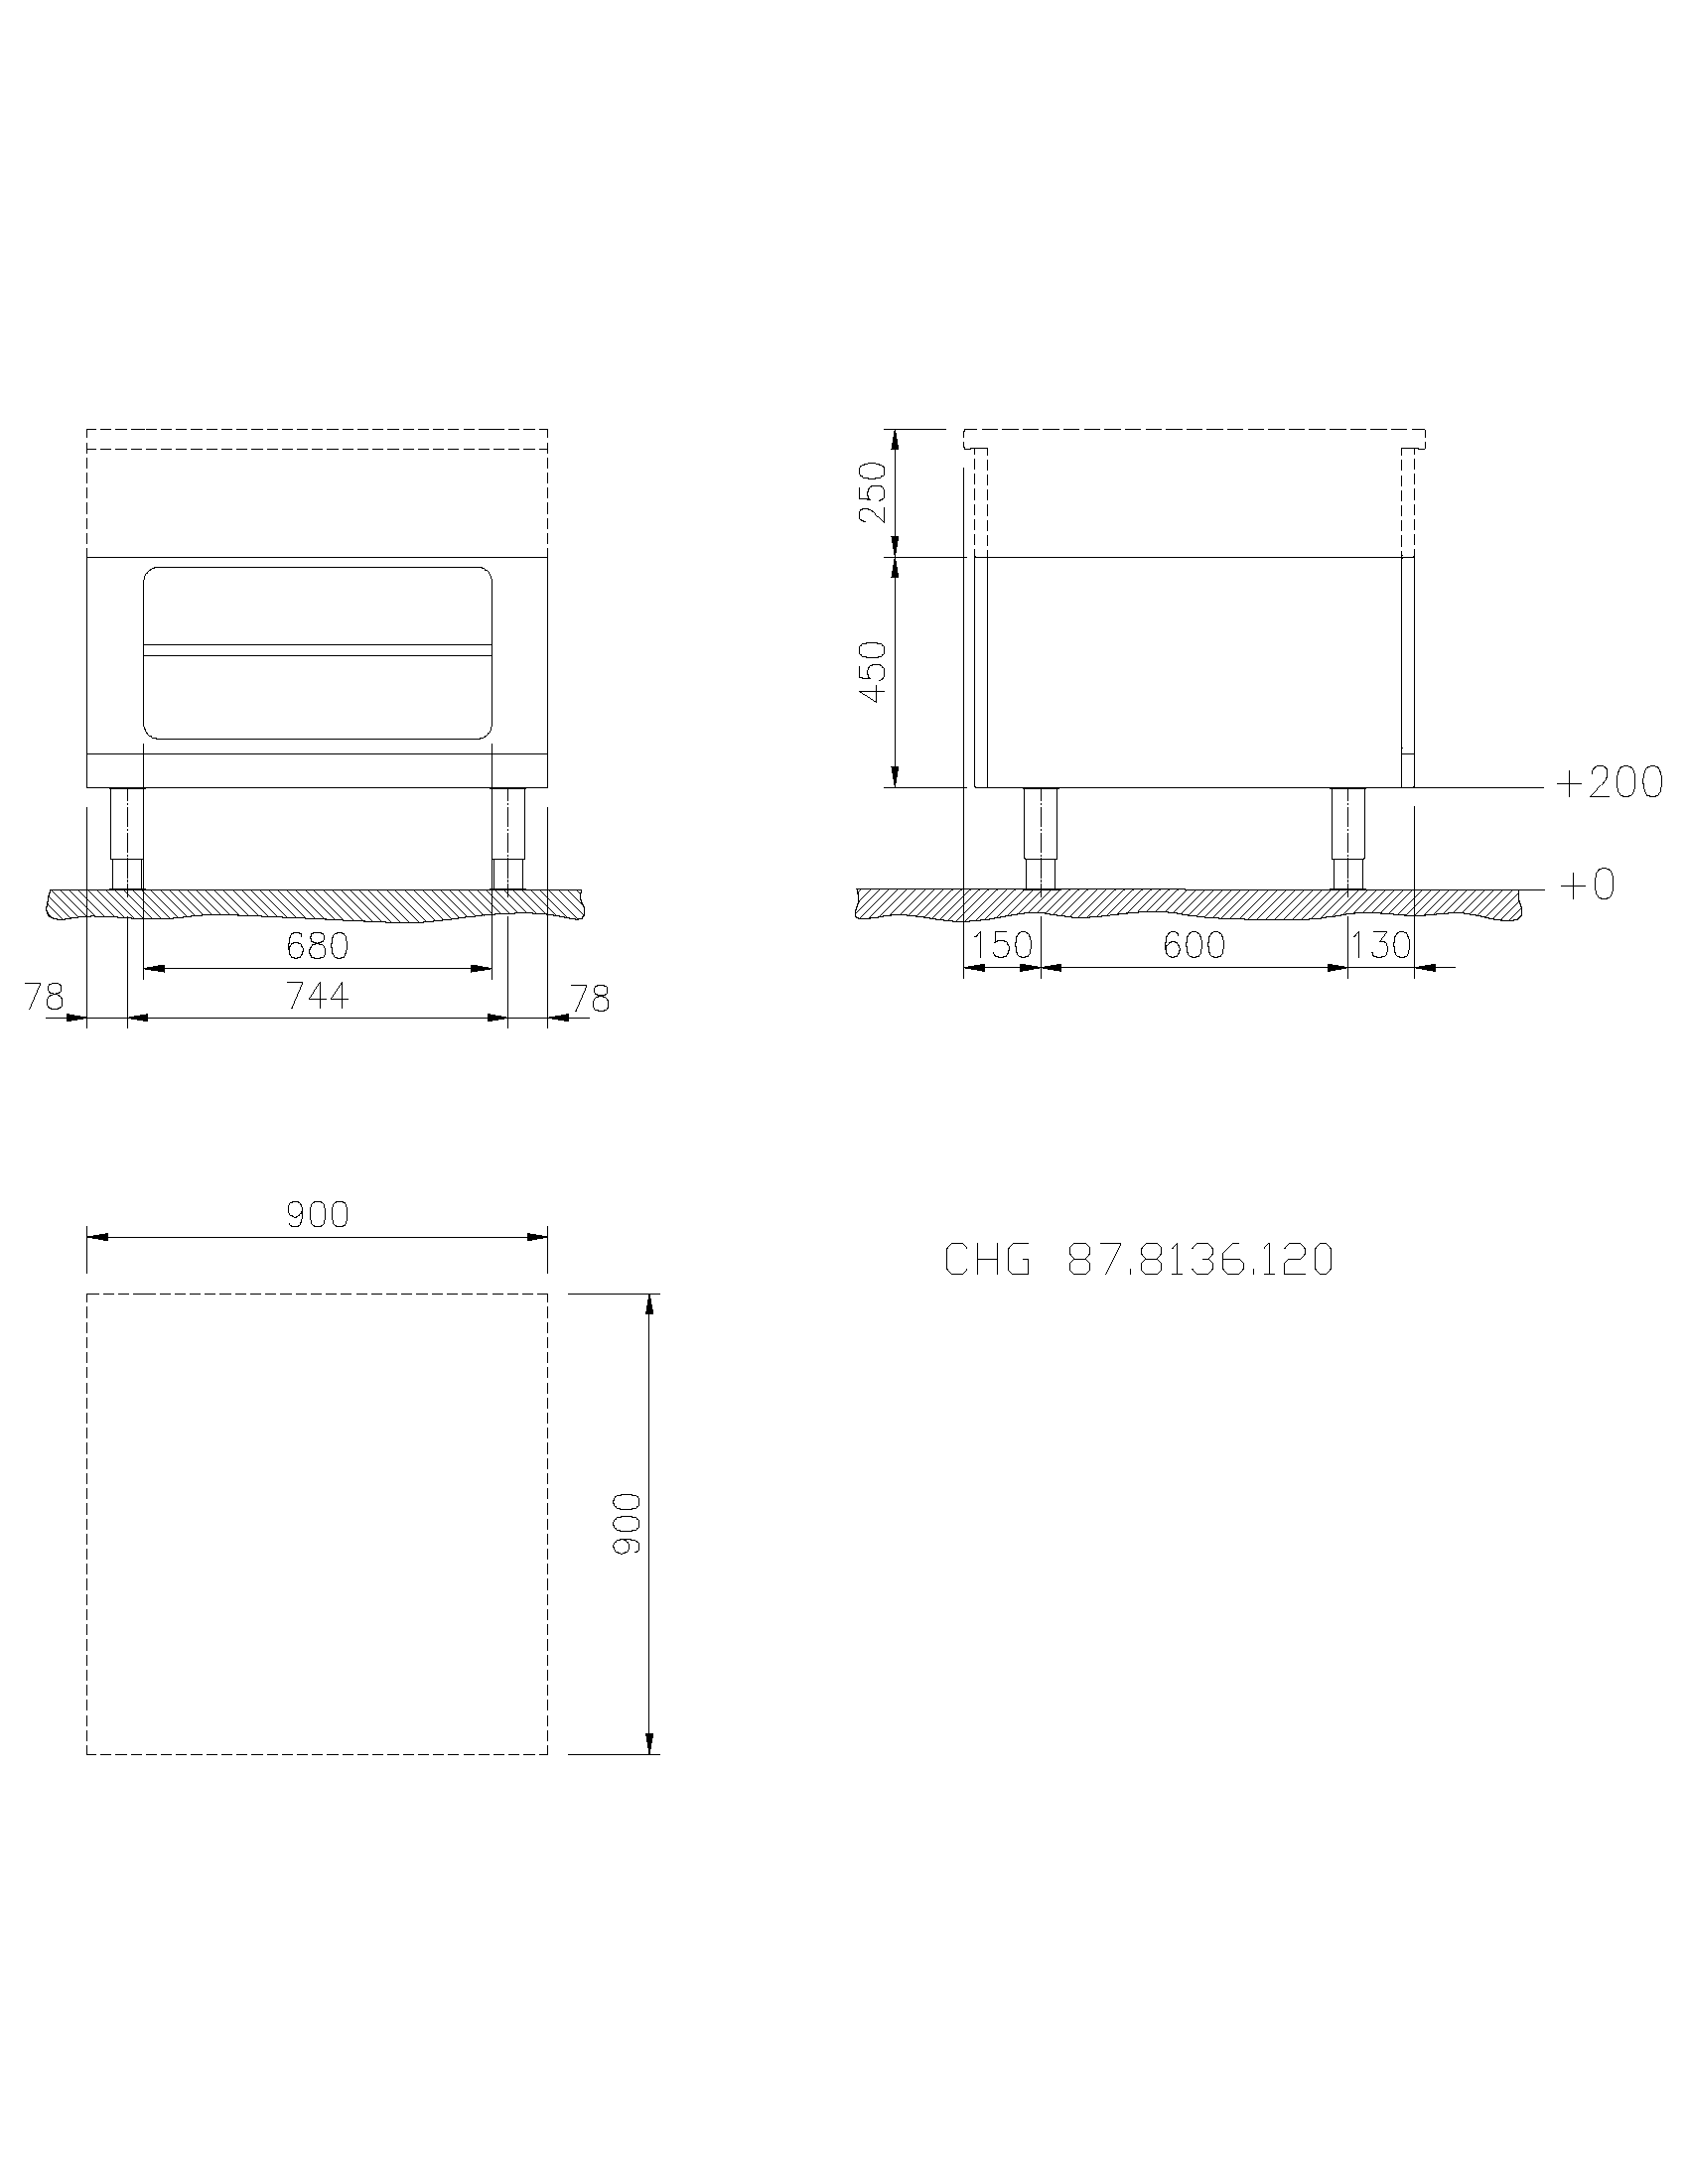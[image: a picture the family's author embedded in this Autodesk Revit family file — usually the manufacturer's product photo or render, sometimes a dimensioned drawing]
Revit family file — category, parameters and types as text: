
# Revit family: QF_ELECTROLUXPROFESSIONAL_589822_MCBFEAE1DM
name_source: partatom
category: Attrezzature speciali
units: mm (PartAtom-declared; Revit-internal decimal feet)

## family parameters
Basato su piano di lavoro = No
Condiviso = No
Punto di calcolo locali = No
Quota connettore circolare = Usa diametro
Sempre verticale = Sì
Taglio con vuoti quando caricato = No
Tipo di parte = Normale

## types (1)
- Standard
    Accessory = Sì
    Cold Water Size = 1"
    Compressed Air Pressure = 0.00 psi
    Compressed Air Size = 0"
    Compressed Air Volume = 0 GPM
    Condensate Return Size = 0"
    Cycle = 50 Hz
    Depth Actual = 900 mm  [stored 2.95276 ft]
    Descrizione = BAINM,1/1GN,TAP(L)1S,500X900X700 MARINE
    Direct Waste Size = 1"
    Gas Input Pressure = 0.0
    Gas KW = 0
    Gas Size = 0"
    HP = 2 HP
    Height Actual = 700 mm  [stored 2.29659 ft]
    Hot Water Size = 1"
    Item Number = 589822
    Length Actual = 500 mm  [stored 1.64042 ft]
    Modello = MCBFEAE1DM
    Phase = 3
    Produttore = Electrolux Professional
    Prospetto di default = 0 mm  [stored 0 ft]
    Refrigerant Compressor Remote = Sì
    Refrigeration Liquid Line Size = 0 mm  [stored 0 ft]
    Refrigeration Suction Line Size = 0 mm  [stored 0 ft]
    Steam Consumption per Hour = 0
    Steam Supply Maximum Pressure = 0.00 psi
    Steam Supply Minimum Pressure = 0.00 psi
    Steam Supply Size = 0"
    URL = https://www.electroluxprofessional.com
    URL Manufacturer = https://www.electroluxprofessional.com
    Volts = 440 V
    Watts = 1500 W
    Weight = 44.00 kg

note: source unit labels omitted for Gas Input Pressure — the stored unit's dimension contradicts the parameter name (converter mislabeling)

note: [stored X ft] marks values corroborated as IEEE doubles in the binary element streams (Revit-internal decimal feet)

## geometry (parser evidence)
native form markers: Blend x3, Sweep x10
no freeform markers — native parametric forms only
